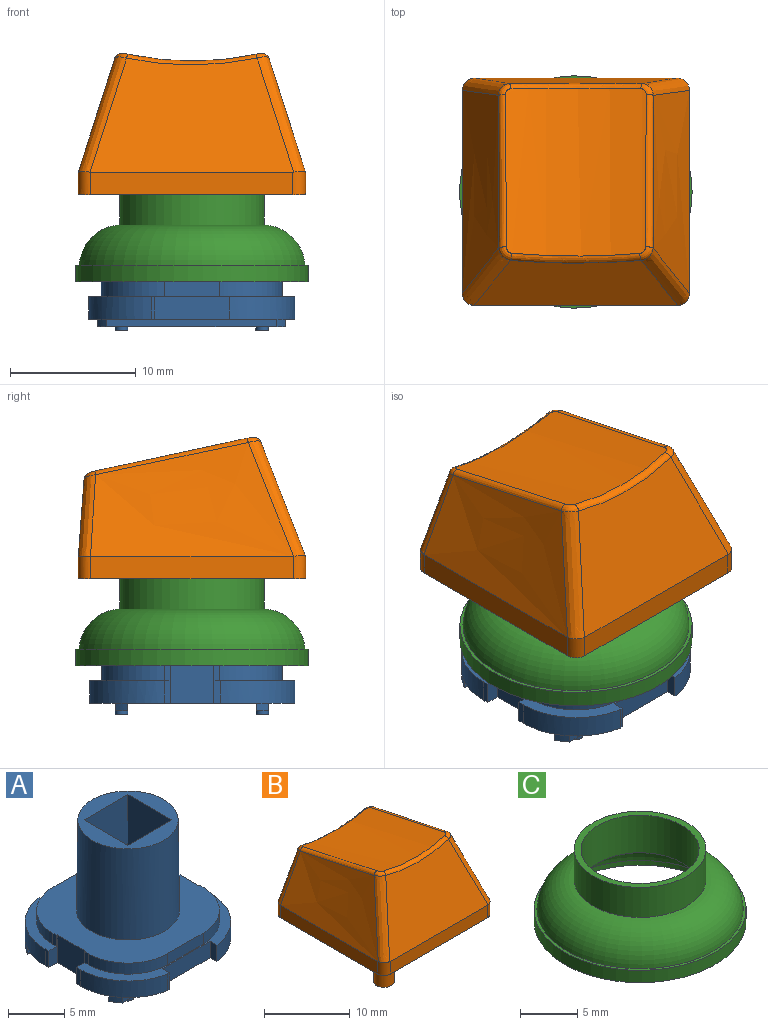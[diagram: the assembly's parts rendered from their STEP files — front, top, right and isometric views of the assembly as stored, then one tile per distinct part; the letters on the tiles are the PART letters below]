
ASSEMBLY  parts=3 mates=2
PART A: 86 faces, bbox 16.4x16.4x13.7 mm
  f0: plane 6x1.8mm, normal (0,1,0), area 10.8mm2, adj f3,f10,f11,f12
  f1: plane 1x1mm, normal (0,0,-1), area 0.8mm2, adj f13
  f2: plane 1x1mm, normal (0,0,-1), area 0.8mm2, adj f14
  f3: plane 1.8x0.85mm, normal (1,0,0), area 1.5mm2, adj f0,f11,f12,f26
  f4: plane 1.2x0.45mm, normal (-1,0,0), area 0.5mm2, adj f5,f11,f27,f28
  f5: revolved ~5x5mm, area 9.4mm2, adj f4,f6,f11,f28
  f6: plane 4.4x1.2mm, normal (0,1,0), area 5.3mm2, adj f5,f7,f11,f28
  f7: revolved ~5x5mm, area 9.4mm2, adj f6,f9,f11,f28
  f8: revolved ~9.8x9.13mm, area 277.6mm2, adj f19,f28
  f9: plane 1.2x0.45mm, normal (1,0,0), area 0.5mm2, adj f7,f11,f28,f29
  f10: plane 1.8x0.85mm, normal (-1,0,0), area 1.5mm2, adj f0,f11,f12,f31
  f11: plane 16.4x6.4mm, normal (0,0,1), area 17.2mm2, adj f0,f3,f4,f5,f6,f7,f9,f10
  f12: plane 13.52x2.05mm, normal (0,0,-1), area 17.2mm2, adj f0,f3,f10,f15,f26,f31
  f13: revolved ~1x1mm, area 0.9mm2, adj f1,f32,f33
  f14: revolved ~1x1mm, area 0.9mm2, adj f2,f33,f34
  f15: plane 13.52x0.6mm, normal (0,1,0), area 8.1mm2, adj f12,f32,f33,f34,f35,f36
  f16: plane 2.8x0.75mm, normal (0,0,-1), area 2.1mm2, adj f40,f41,f42,f43
  f17: plane 2.8x0.75mm, normal (0,0,-1), area 2.1mm2, adj f44,f45,f46,f47
  f18: plane 2.8x0.75mm, normal (0,0,-1), area 2.1mm2, adj f48,f49,f50,f51
  f19: plane 8.9x8.9mm, normal (0,0,1), area 32mm2, adj f8,f43,f47,f51,f52
  f20: plane 2.8x0.75mm, normal (0,0,-1), area 2.1mm2, adj f37,f38,f39,f52
  f21: revolved ~5x5mm, area 9.4mm2, adj f22,f24,f28,f55
  f22: plane 4.4x1.2mm, normal (0,-1,0), area 5.3mm2, adj f21,f23,f28,f55
  f23: revolved ~5x5mm, area 9.4mm2, adj f22,f28,f53,f55
  f24: plane 1.2x0.45mm, normal (1,0,0), area 0.5mm2, adj f21,f28,f55,f57
  f25: plane 1.8x0.45mm, normal (-1,0,0), area 0.8mm2, adj f11,f26,f27,f58
  f26: revolved ~5.95x5.2mm, area 15.5mm2, adj f3,f11,f12,f25,f35,f58
  f27: plane 3x1.1mm, normal (0,-1,0), area 2.1mm2, adj f4,f11,f25,f28,f58,f59,f72
  f28: plane 14.4x14.4mm, normal (0,0,1), area 119.7mm2, adj f4,f5,f6,f7,f8,f9,f21,f22
  f29: plane 3x1.1mm, normal (0,-1,0), area 2.1mm2, adj f9,f11,f28,f30,f60,f61,f72
  f30: plane 1.8x0.45mm, normal (1,0,0), area 0.8mm2, adj f11,f29,f31,f61
  f31: revolved ~5.95x5.2mm, area 15.5mm2, adj f10,f11,f12,f30,f36,f61
  f32: plane 1.86x1mm, normal (0,0,-1), area 1.1mm2, adj f13,f15,f36,f62
  f33: plane 11.2x1mm, normal (0,0,-1), area 10.4mm2, adj f13,f14,f15,f62
  f34: plane 1.85x1mm, normal (0,0,-1), area 1.1mm2, adj f14,f15,f35,f62
  f35: revolved ~1x0.69mm, area 0.7mm2, adj f15,f26,f34,f62
  f36: revolved ~1x0.69mm, area 0.7mm2, adj f15,f31,f32,f62
  f37: plane 5.9x0.75mm, normal (0,1,0), area 4.4mm2, adj f20,f38,f52,f63
  f38: plane 5.9x2.8mm, normal (1,0,0), area 16.5mm2, adj f20,f37,f39,f63
  f39: plane 5.9x0.75mm, normal (0,-1,0), area 4.4mm2, adj f20,f38,f52,f63
  f40: plane 5.9x0.75mm, normal (1,0,0), area 4.4mm2, adj f16,f41,f43,f63
  f41: plane 5.9x2.8mm, normal (0,-1,0), area 16.5mm2, adj f16,f40,f42,f63
  f42: plane 5.9x0.75mm, normal (-1,0,0), area 4.4mm2, adj f16,f41,f43,f63
  f43: plane 12.8x5.5mm, normal (0,-1,0), area 53.9mm2, adj f16,f19,f40,f42,f47,f52,f63
  f44: plane 5.9x0.75mm, normal (0,-1,0), area 4.4mm2, adj f17,f45,f47,f63
  f45: plane 5.9x2.8mm, normal (-1,0,0), area 16.5mm2, adj f17,f44,f46,f63
  f46: plane 5.9x0.75mm, normal (0,1,0), area 4.4mm2, adj f17,f45,f47,f63
  f47: plane 12.8x5.5mm, normal (-1,0,0), area 53.9mm2, adj f17,f19,f43,f44,f46,f51,f63
  f48: plane 5.9x0.75mm, normal (-1,0,0), area 4.4mm2, adj f18,f49,f51,f63
  f49: plane 5.9x2.8mm, normal (0,1,0), area 16.5mm2, adj f18,f48,f50,f63
  f50: plane 5.9x0.75mm, normal (1,0,0), area 4.4mm2, adj f18,f49,f51,f63
  f51: plane 12.8x5.5mm, normal (0,1,0), area 53.9mm2, adj f18,f19,f47,f48,f50,f52,f63
  f52: plane 12.8x5.5mm, normal (1,0,0), area 53.9mm2, adj f19,f20,f37,f39,f43,f51,f63
  f53: plane 1.2x0.45mm, normal (-1,0,0), area 0.5mm2, adj f23,f28,f55,f64
  f54: plane 1.8x0.2mm, normal (0,-1,0), area 0.4mm2, adj f55,f66,f70,f77
  f55: plane 16.4x6.45mm, normal (0,0,1), area 17.6mm2, adj f21,f22,f23,f24,f53,f54,f56,f57
  f56: plane 1.8x0.45mm, normal (1,0,0), area 0.8mm2, adj f55,f57,f69,f71
  f57: plane 3x1.1mm, normal (0,1,0), area 2.1mm2, adj f24,f28,f55,f56,f60,f71,f72
  f58: plane 3.35x1.93mm, normal (0,0,-1), area 3.5mm2, adj f25,f26,f27,f62,f72
  f59: plane 3.5x3mm, normal (-1,0,0), area 10.5mm2, adj f27,f28,f64,f72
  f60: plane 3.5x3mm, normal (1,0,0), area 10.5mm2, adj f28,f29,f57,f72
  f61: plane 3.35x1.93mm, normal (0,0,-1), area 3.5mm2, adj f29,f30,f31,f62,f72
  f62: plane 14.91x0.6mm, normal (0,-1,0), area 8.9mm2, adj f32,f33,f34,f35,f36,f58,f61,f72
  f63: plane 9.2x9.2mm, normal (0,0,-1), area 27.8mm2, adj f37,f38,f39,f40,f41,f42,f43,f44
  f64: plane 3x1.1mm, normal (0,1,0), area 2.1mm2, adj f28,f53,f55,f59,f65,f72,f73
  f65: plane 1.8x0.53mm, normal (-1,0,0), area 1mm2, adj f55,f64,f70,f73
  f66: plane 1.8x0.9mm, normal (1,0,0), area 1.6mm2, adj f54,f55,f67,f77
  f67: plane 6x1.8mm, normal (0,-1,0), area 10.8mm2, adj f55,f66,f68,f77
  f68: plane 1.8x0.85mm, normal (-1,0,0), area 1.5mm2, adj f55,f67,f69,f77
  f69: revolved ~5.95x5.2mm, area 15.5mm2, adj f55,f56,f68,f71,f75,f77
  f70: revolved ~5.92x5mm, area 15.2mm2, adj f54,f55,f65,f73,f77,f78
  f71: plane 3.35x1.93mm, normal (0,0,-1), area 3.5mm2, adj f56,f57,f69,f72,f79
  f72: plane 14.4x10.2mm, normal (0,0,-1), area 76.3mm2, adj f27,f29,f57,f58,f59,f60,f61,f62
  f73: plane 3.35x1.93mm, normal (0,0,-1), area 3.6mm2, adj f64,f65,f70,f72,f79
  f74: plane 1x1mm, normal (0,0,-1), area 0.8mm2, adj f80
  f75: revolved ~1x0.69mm, area 0.7mm2, adj f69,f76,f79,f81
  f76: plane 1.86x1mm, normal (0,0,-1), area 1.1mm2, adj f75,f79,f80,f81
  f77: plane 13.59x2.1mm, normal (0,0,-1), area 17.5mm2, adj f54,f66,f67,f68,f69,f70,f81
  f78: revolved ~1x0.67mm, area 0.7mm2, adj f70,f79,f81,f82
  f79: plane 14.95x0.6mm, normal (0,1,0), area 9mm2, adj f71,f72,f73,f75,f76,f78,f82,f83
  f80: revolved ~1x1mm, area 0.9mm2, adj f74,f76,f83
  f81: plane 13.59x0.6mm, normal (0,-1,0), area 8.2mm2, adj f75,f76,f77,f78,f82,f83
  f82: plane 1.9x1mm, normal (0,0,-1), area 1.2mm2, adj f78,f79,f81,f84
  f83: plane 11.2x1mm, normal (0,0,-1), area 10.4mm2, adj f79,f80,f81,f84
  f84: revolved ~1x1mm, area 0.9mm2, adj f82,f83,f85
  f85: plane 1x1mm, normal (0,0,-1), area 0.8mm2, adj f84
PART B: 42 faces, bbox 21.1x23x23.7 mm
  f0: plane 18.1x18.1mm, normal (0,0,-1), area 67.5mm2, adj f1,f2,f3,f4,f10,f12,f14,f16
  f1: plane 16.1x1.8mm, normal (1,0,0), area 29mm2, adj f0,f8,f10,f16
  f2: plane 16.11x1.81mm, normal (0,1,0), area 29mm2, adj f0,f5,f14,f15,f16,f17
  f3: plane 16.1x1.8mm, normal (-1,0,0), area 29mm2, adj f0,f6,f12,f14
  f4: plane 16.1x1.8mm, normal (0,-1,0), area 29mm2, adj f0,f7,f10,f12
  f5: plane 15.98x6.12mm, normal (0,1,0.07), area 77mm2, adj f2,f15,f17,f20
  f6: bspline ~18.1x9.7mm, area 119.5mm2, adj f3,f12,f13,f14,f15,f19
  f7: plane 16.23x9.1mm, normal (0,-0.93,0.36), area 126mm2, adj f4,f10,f11,f12,f13,f23
  f8: bspline ~18.1x9.7mm, area 119.6mm2, adj f1,f10,f11,f16,f17,f24
  f9: cylinder r=22.9mm len=13.26mm, axis (0,0.98,-0.21), area 150.5mm2, adj f18,f19,f20,f21,f22,f23,f24,f25
  f10: cylinder r=1mm len=1.86mm, axis (0,0,-1), area 2.9mm2, adj f0,f1,f4,f7,f8,f11
  f11: bspline ~11.76x5.48mm, area 15.2mm2, adj f7,f8,f10,f25
  f12: cylinder r=1mm len=1.86mm, axis (0,0,1), area 2.9mm2, adj f0,f3,f4,f6,f7,f13
  f13: bspline ~11.82x5.5mm, area 15.2mm2, adj f6,f7,f12,f21
  f14: cylinder r=1mm len=1.81mm, axis (0,0,-1), area 2.8mm2, adj f0,f2,f3,f6,f15
  f15: bspline ~8.75x4.63mm, area 10.5mm2, adj f2,f5,f6,f14,f18
  f16: cylinder r=1mm len=1.81mm, axis (0,0,1), area 2.8mm2, adj f0,f1,f2,f8,f17
  f17: bspline ~8.72x4.61mm, area 10.5mm2, adj f2,f5,f8,f16,f22
  f18: bspline ~1.16x1.04mm, area 0.7mm2, adj f9,f15,f19,f20
  f19: bspline ~19.37x4.53mm, area 9.1mm2, adj f6,f9,f18,f21
  f20: bspline ~10.57x1.07mm, area 6.8mm2, adj f5,f9,f18,f22
  f21: bspline ~1.24x1.16mm, area 0.9mm2, adj f9,f13,f19,f23
  f22: bspline ~1.18x0.98mm, area 0.7mm2, adj f9,f17,f20,f24
  f23: bspline ~10.39x0.86mm, area 7.3mm2, adj f7,f9,f21,f25
  f24: bspline ~19.36x4.52mm, area 9.1mm2, adj f8,f9,f22,f25
  f25: bspline ~1.33x1.09mm, area 0.9mm2, adj f9,f11,f23,f24
  f26: plane 16.13x1.68mm, normal (-1,0,0), area 26.1mm2, adj f0,f27,f29,f32,f33
  f27: plane 16.1x1.76mm, normal (0,-1,0), area 28.4mm2, adj f0,f26,f28,f30,f31,f33
  f28: plane 16.13x1.68mm, normal (1,0,0), area 26.1mm2, adj f0,f27,f29,f31,f32
  f29: plane 16.1x1.61mm, normal (0,1,0), area 25.9mm2, adj f0,f26,f28,f32
  f30: plane 16.32x6.11mm, normal (0,-1,-0.07), area 72.4mm2, adj f27,f31,f33,f34
  f31: offset ~20.1x11.7mm, area 111mm2, adj f27,f28,f30,f32,f34
  f32: plane 16.29x8.73mm, normal (0,0.93,-0.36), area 118.5mm2, adj f26,f28,f29,f31,f33,f34
  f33: offset ~20.1x11.7mm, area 111mm2, adj f26,f27,f30,f32,f34
  f34: cylinder r=23.9mm len=12.45mm, axis (0,0.98,-0.21), area 108mm2, adj f30,f31,f32,f33,f36,f37,f38,f39
  f35: plane 5.3x5.3mm, normal (0,0,-1), area 23.6mm2, adj f36,f37,f38,f39,f40
  f36: plane 14.26x5.36mm, normal (0,1,0), area 74.7mm2, adj f34,f35,f37,f38
  f37: plane 15.34x5.3mm, normal (1,0,0), area 78.3mm2, adj f34,f35,f36,f39
  f38: plane 15.34x5.3mm, normal (-1,0,0), area 78.3mm2, adj f34,f35,f36,f39
  f39: plane 15.41x5.36mm, normal (0,-1,0), area 80.8mm2, adj f34,f35,f37,f38
  f40: cylinder r=1.2mm len=3.5mm, axis (0,0,1), area 26.4mm2, adj f35,f41
  f41: plane 2.4x2.4mm, normal (0,0,-1), area 4.5mm2, adj f40
PART C: 9 faces, bbox 19.5x19.5x7.7 mm
  f0: cylinder r=9.25mm len=18.5mm, axis (0,0,1), area 76.2mm2, adj f1,f8
  f1: plane 18.5x18.5mm, normal (0,0,-1), area 41.8mm2, adj f0,f2
  f2: cylinder r=8.5mm len=17mm, axis (0,0,1), area 27.5mm2, adj f1,f3
  f3: torus R=5.16mm, axis (0,0,1), area 232.3mm2, adj f2,f4
  f4: cylinder r=5.15mm len=10.3mm, axis (0,0,1), area 129.4mm2, adj f3,f5
  f5: plane 11.5x11.5mm, normal (0,0,1), area 20.5mm2, adj f4,f6
  f6: cylinder r=5.75mm len=11.5mm, axis (0,0,1), area 115.6mm2, adj f5,f7
  f7: torus R=5.6mm, axis (0,0,1), area 243.6mm2, adj f6,f8
  f8: plane 18.5x18.5mm, normal (0,0,1), area 14.3mm2, adj f0,f7
PLACE A at identity fixed
PLACE B t=(0,0,9.9)mm
PLACE C t=(0,0,3)mm
MATE fastened A.f19 <-> B.f40  axis (0,0,1) through (0,0,12.8)mm
MATE fastened A.f28 <-> C.f0  axis (0,0,1) through (0,0,3)mm
